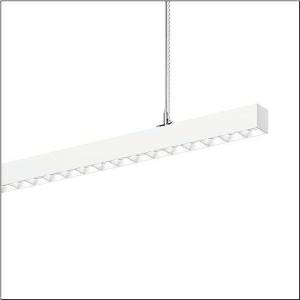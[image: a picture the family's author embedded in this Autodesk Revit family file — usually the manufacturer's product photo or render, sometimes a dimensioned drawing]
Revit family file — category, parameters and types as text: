
# Revit family: silica_r__21_51mx36da37wb_45fb
name_source: partatom
category: Lighting Fixtures
units: mm (PartAtom-declared; Revit-internal decimal feet)

## family parameters
Cut with Voids When Loaded = No
Host = Face
Light Source = No
Part Type = Normal
Room Calculation Point = No
Round Connector Dimension = Use Diameter
Shared = No

## types (1)
- --- (1 x LED, 7060 lm, 43 W, 3000K)
    Apparent Load = 43 VA
    CIE Flux Codes = 83 98 100 61 100
    Color Rendering = 80
    Color Temperature = 3000K
    Default Elevation = 1800 mm
    Description = Silica® 21, office luminaire, primary light control with darklight reflector, of PMMA, white, CAT 2 (L<= 3000cd/m²), light emission: direct/indirect distribution, primary light characteristic: symmetric, installation type: suspended mounting, LED, rated luminous flux: 7.060lm, luminous efficacy: 164lm/W, light colour: 830, colour temperature: 3000K, control gear: DALI 2, with terminal, 3+2-pole, max. 2.5mm², mains connection: 220..240V, AC, 50/60Hz, rated input power: 43W, luminaire housing, of aluminium, traffic white (RAL 9016), length: 1.204mm, width: 53mm, height: 53mm, protection rating (complete): IP20, insulation class (complete): insulation class I (protective earthing), certification: CE, permissible operating ambient temperature: 0..+35°C, standard: EN 50419, packaging unit: 1 piece
    Height = 53 mm
    Lamp = 1 x LED
    Lamp Light Flux = 7060 lm
    Lamp Power = 43 W
    Lamp count = 1
    Length = 1204 mm
    Luminous efficacy = 164 lm/W
    Manufacturer = Siteco
    ModVariant = No
    Model = 51MX36DA37WB
    Mounting Place = Ceiling
    Mounting Type = Pendant
    Number of Poles = 1
    OnlyDefault = Yes
    Power Factor = 1
    Product Name = Silica® 21
    Product group = office luminaire | ceiling pendant
    ProductGroupID = 904
    Protection Class = Protection class I
    Protection Degree = IP 20
    RLX_Detail_Level = 1
    RLX_Emergency_Light_Flux = 0 lm
    RLX_Emergency_Type = 0
    RLX_Emergency_Type_DB = No
    RlxData = <blob elided: 40973 chars, md5=5154c35e>
    Socket = socket
    Standby Power = 0 W
    System Light Flux = 7060 lm
    System Power = 43 W
    Type Comments = factory setting: luminous flux: 100 % | dim-lin: 254 | 359 mA
    Type Image = l_1335921.jpg
    URL = http://relux.com
    VarID = @adj_121354
    Voltage = 0 V
    Weight = 0.00 kg
    Width = 53 mm

## geometry (parser evidence)
native form markers: Blend x4, Sweep x13
no freeform markers — native parametric forms only
